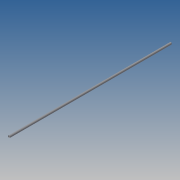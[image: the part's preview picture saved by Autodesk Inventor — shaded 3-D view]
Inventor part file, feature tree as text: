
AUTODESK INVENTOR PART (.ipt)
format: ipt  version: 2014 SP1 (Build 180222100, 222)  size: 74,240 bytes
history: native  units: in
note: dims shown in document units (in); Inventor stores cm internally (conversion verified against a paired STEP export)
features: extrude x1, sketch x1
ambient origin geometry x8: Origin, YZ Plane, XZ Plane, XY Plane, X Axis, Y Axis, Z Axis, Center Point
bodies: Solid1 (feature_tree)
feature tree (2):
  extrude  "Extrusion1"  Depth=472.4409in
  sketch  "Sketch1"  dims[d1=0.2in d2=6.0in d3=472.4409in d4=0.0in]
